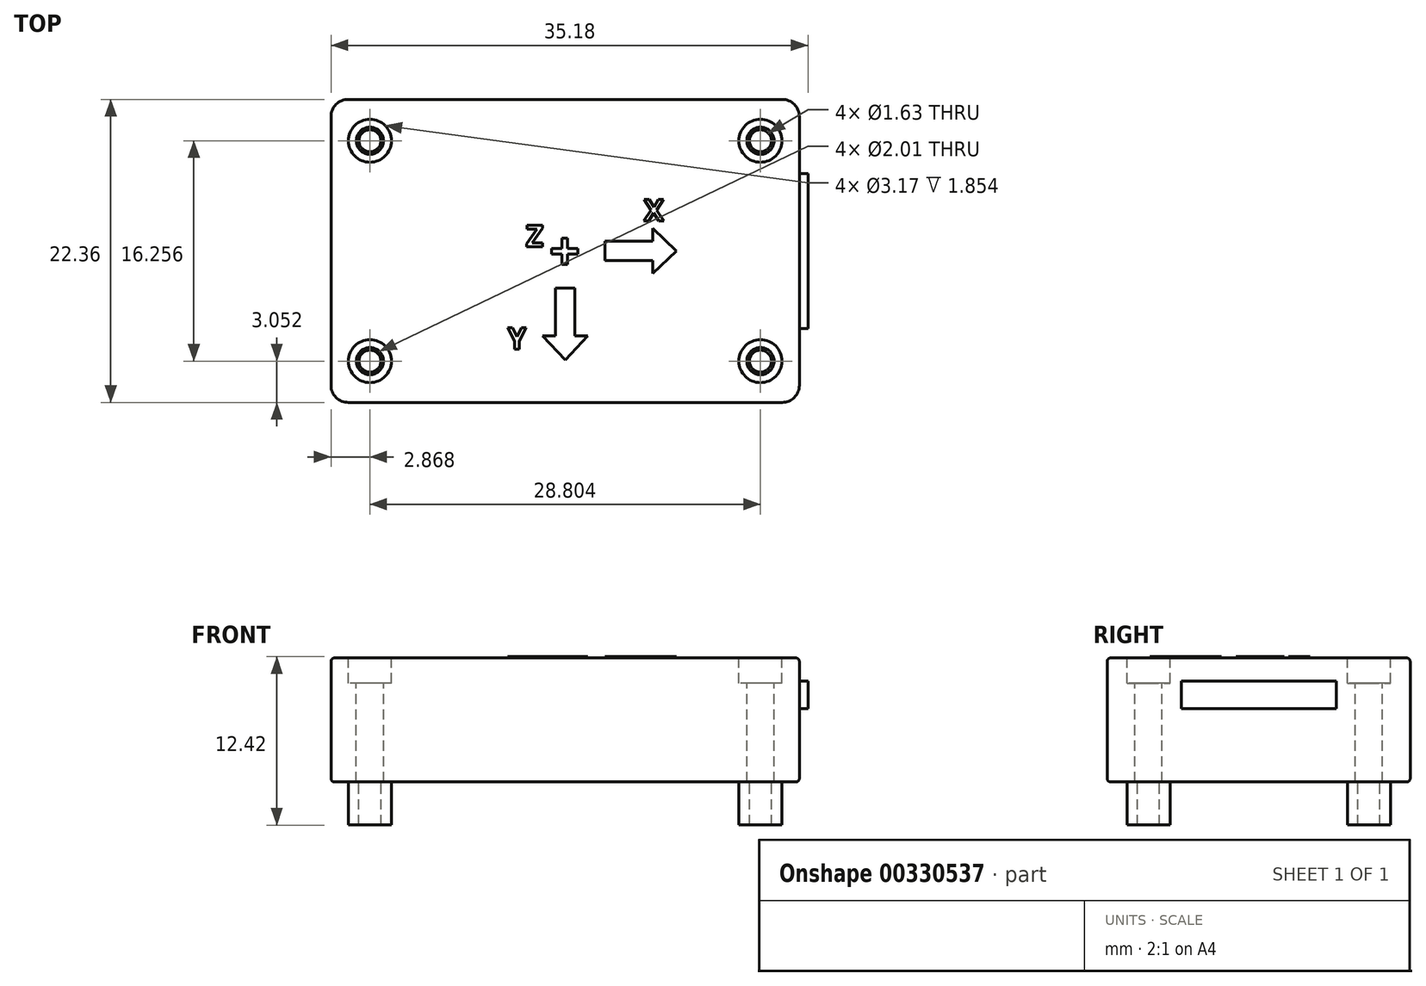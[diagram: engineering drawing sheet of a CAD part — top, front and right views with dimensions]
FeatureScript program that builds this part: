
annotation { "Feature Type Name" : "Feature", "Feature Type Description" : "" }
export const myFeature = defineFeature(function(context is Context, id is Id, definition is map)
    precondition{}
    {
        {
            var Q0;
            Q0=qCreatedBy(makeId("Top.planeOp"),FACE);
            var sketch = newSketch(context, id + "F0", { "sketchPlane" : qUnion([Q0])});
            skLineSegment(sketch, "E0.bottom", {"start": v(16, -11.18) * mm, "end": v(-16, -11.18) * mm});
            skLineSegment(sketch, "E0.top", {"start": v(16, 11.18) * mm, "end": v(-16, 11.18) * mm});
            skLineSegment(sketch, "E0.left", {"start": v(17.27, -9.9) * mm, "end": v(17.27, 9.9) * mm});
            skLineSegment(sketch, "E0.right", {"start": v(-17.27, -9.9) * mm, "end": v(-17.27, 9.9) * mm});
            skPoint(sketch, "E0.middle", {"position": v(0, 0) * mm});
            skPoint(sketch, "E1.visualSharp", {"position": v(-17.27, 11.18) * mm});
            skArc(sketch, "E1.filletArc", {"start": v(-16, 11.18) * mm, "mid": v(-16.9, 10.8) * mm, "end": v(-17.27, 9.9) * mm});
            skPoint(sketch, "E2.visualSharp", {"position": v(17.27, 11.18) * mm});
            skArc(sketch, "E2.filletArc", {"start": v(17.27, 9.9) * mm, "mid": v(16.9, 10.8) * mm, "end": v(16, 11.18) * mm});
            skPoint(sketch, "E3.visualSharp", {"position": v(17.27, -11.18) * mm});
            skArc(sketch, "E3.filletArc", {"start": v(16, -11.18) * mm, "mid": v(16.9, -10.8) * mm, "end": v(17.27, -9.9) * mm});
            skPoint(sketch, "E4.visualSharp", {"position": v(-17.27, -11.18) * mm});
            skArc(sketch, "E4.filletArc", {"start": v(-17.27, -9.9) * mm, "mid": v(-16.9, -10.8) * mm, "end": v(-16, -11.18) * mm});
            skSolve(sketch);
        }
        {
            var Q0;
            Q0 = qSketchRegion(id + "F0", true);
            extrude(context, id + "F1", {"entities" : qUnion([Q0]), "depth" : 9.14 * mm, "offsetDistance" : 25.4 * mm});
        }
        {
            var Q0;
            Q0=makeQuery(id+"F1.opExtrude","CAP_EDGE",EDGE,{"disambiguationData":[OSD([sQuery(id+"F0.wireOp",EDGE,"E0.bottom")])],"isStart":false});
            var Q1;
            Q1=makeQuery(id+"F1.opExtrude","CAP_FACE",FACE,{"disambiguationData":[OSD([sQuery(id+"F0.wireOp",EDGE,"E0.bottom"),sQuery(id+"F0.wireOp",EDGE,"E0.top"),sQuery(id+"F0.wireOp",EDGE,"E0.left"),sQuery(id+"F0.wireOp",EDGE,"E0.right"),sQuery(id+"F0.wireOp",EDGE,"E1.filletArc"),sQuery(id+"F0.wireOp",EDGE,"E2.filletArc"),sQuery(id+"F0.wireOp",EDGE,"E3.filletArc"),sQuery(id+"F0.wireOp",EDGE,"E4.filletArc")])],"isStart":true});
            fillet(context, id + "F2", {"entities" : qUnion([Q0, Q1]), "radius" : 0.25 * mm, "tangentPropagation" : true, "allowEdgeOverflow" : false});
        }
        {
            var Q0;
            Q0=makeQuery(id+"F1.opExtrude","CAP_FACE",FACE,{"disambiguationData":[OSD([sQuery(id+"F0.wireOp",EDGE,"E0.bottom"),sQuery(id+"F0.wireOp",EDGE,"E0.top"),sQuery(id+"F0.wireOp",EDGE,"E0.left"),sQuery(id+"F0.wireOp",EDGE,"E0.right"),sQuery(id+"F0.wireOp",EDGE,"E1.filletArc"),sQuery(id+"F0.wireOp",EDGE,"E2.filletArc"),sQuery(id+"F0.wireOp",EDGE,"E3.filletArc"),sQuery(id+"F0.wireOp",EDGE,"E4.filletArc")])],"isStart":false});
            var sketch = newSketch(context, id + "F3", { "sketchPlane" : qUnion([Q0])});
            skLineSegment(sketch, "E5", {"start": v(0, 10.92) * mm, "end": v(0, -10.92) * mm, "construction": true});
            skLineSegment(sketch, "E6", {"start": v(-17.02, 0) * mm, "end": v(17.52, 0) * mm, "construction": true});
            skPoint(sketch, "E6.endSnap0", {"position": v(17.02, 0) * mm});
            skCircle(sketch, "E7", {"center": v(-14.4, 8.13) * mm, "radius": 1 * mm});
            skCircle(sketch, "E8.MirrorC", {"center": v(14.4, 8.13) * mm, "radius": 1 * mm});
            skLineSegment(sketch, "E9.MirrorCS", {"start": v(17.02, 0) * mm, "end": v(-17.52, 0) * mm, "construction": true});
            skCircle(sketch, "E10.MirrorC", {"center": v(-14.4, -8.13) * mm, "radius": 1 * mm});
            skCircle(sketch, "E11.MirrorC", {"center": v(14.4, -8.13) * mm, "radius": 1 * mm});
            skSolve(sketch);
        }
        {
            var Q0;
            Q0 = qSketchRegion(id + "F3", true);
            extrude(context, id + "F4", {"entities" : qUnion([Q0]), "operationType" : NewBodyOperationType.REMOVE, "endBound" : BoundingType.THROUGH_ALL, "oppositeDirection" : true, "depth" : 25.4 * mm, "offsetDistance" : 25.4 * mm});
        }
        {
            var Q0;
            Q0=makeQuery(id+"F1.opExtrude","CAP_FACE",FACE,{"disambiguationData":[OSD([sQuery(id+"F0.wireOp",EDGE,"E0.bottom"),sQuery(id+"F0.wireOp",EDGE,"E0.top"),sQuery(id+"F0.wireOp",EDGE,"E0.left"),sQuery(id+"F0.wireOp",EDGE,"E0.right"),sQuery(id+"F0.wireOp",EDGE,"E1.filletArc"),sQuery(id+"F0.wireOp",EDGE,"E2.filletArc"),sQuery(id+"F0.wireOp",EDGE,"E3.filletArc"),sQuery(id+"F0.wireOp",EDGE,"E4.filletArc")])],"isStart":false});
            var sketch = newSketch(context, id + "F5", { "sketchPlane" : qUnion([Q0])});
            skCircle(sketch, "E12", {"center": v(-14.4, 8.13) * mm, "radius": 1.59 * mm});
            skCircle(sketch, "E13", {"center": v(14.4, 8.13) * mm, "radius": 1.59 * mm});
            skCircle(sketch, "E14", {"center": v(14.4, -8.13) * mm, "radius": 1.59 * mm});
            skCircle(sketch, "E15", {"center": v(-14.4, -8.13) * mm, "radius": 1.59 * mm});
            skSolve(sketch);
        }
        {
            var Q0;
            Q0 = qSketchRegion(id + "F5", true);
            extrude(context, id + "F6", {"entities" : qUnion([Q0]), "operationType" : NewBodyOperationType.REMOVE, "oppositeDirection" : true, "depth" : 1.85 * mm, "offsetDistance" : 25.4 * mm});
        }
        {
            var Q0;
            Q0=makeQuery(id+"F1.opExtrude","SWEPT_FACE",FACE,{"disambiguationData":[OSD([sQuery(id+"F0.wireOp",EDGE,"E0.left")])]});
            var sketch = newSketch(context, id + "F7", { "sketchPlane" : qUnion([Q0])});
            skLineSegment(sketch, "E16", {"start": v(0, 8.9) * mm, "end": v(0, 0) * mm, "construction": true});
            skLineSegment(sketch, "E17", {"start": v(-11.07, 4.57) * mm, "end": v(11.58, 4.57) * mm, "construction": true});
            skPoint(sketch, "E17.startSnap0", {"position": v(-9.9, 4.57) * mm});
            skLineSegment(sketch, "E18.bottom", {"start": v(5.71, 5.4) * mm, "end": v(-5.71, 5.4) * mm});
            skLineSegment(sketch, "E18.top", {"start": v(5.71, 7.43) * mm, "end": v(-5.71, 7.43) * mm});
            skLineSegment(sketch, "E18.left", {"start": v(5.71, 5.4) * mm, "end": v(5.71, 7.43) * mm});
            skLineSegment(sketch, "E18.right", {"start": v(-5.71, 5.4) * mm, "end": v(-5.71, 7.43) * mm});
            skPoint(sketch, "E18.middle", {"position": v(0, 6.42) * mm});
            skSolve(sketch);
        }
        {
            var Q0;
            Q0 = qSketchRegion(id + "F7", true);
            extrude(context, id + "F8", {"entities" : qUnion([Q0]), "depth" : 0.64 * mm, "offsetDistance" : 25.4 * mm});
        }
        {
            var Q0;
            Q0=makeQuery(id+"F1.opExtrude","CAP_FACE",FACE,{"disambiguationData":[OSD([sQuery(id+"F0.wireOp",EDGE,"E0.bottom"),sQuery(id+"F0.wireOp",EDGE,"E0.top"),sQuery(id+"F0.wireOp",EDGE,"E0.left"),sQuery(id+"F0.wireOp",EDGE,"E0.right"),sQuery(id+"F0.wireOp",EDGE,"E1.filletArc"),sQuery(id+"F0.wireOp",EDGE,"E2.filletArc"),sQuery(id+"F0.wireOp",EDGE,"E3.filletArc"),sQuery(id+"F0.wireOp",EDGE,"E4.filletArc")])],"isStart":false});
            var sketch = newSketch(context, id + "F9", { "sketchPlane" : qUnion([Q0])});
            skText(sketch, "E19", { "text": "X", "fontName": "OpenSans-Bold.ttf"});
            skLineSegment(sketch, "E20", {"start": v(0, 0) * mm, "end": v(5.39, 0) * mm, "construction": true});
            skLineSegment(sketch, "E21", {"start": v(0, 0) * mm, "end": v(0, -3.11) * mm, "construction": true});
            skLineSegment(sketch, "E22", {"start": v(2.92, 0) * mm, "end": v(2.92, 0.72) * mm});
            skLineSegment(sketch, "E23", {"start": v(2.92, 0.72) * mm, "end": v(6.45, 0.72) * mm});
            skLineSegment(sketch, "E24", {"start": v(6.45, 0.72) * mm, "end": v(6.45, 1.67) * mm});
            skLineSegment(sketch, "E25", {"start": v(6.45, 1.67) * mm, "end": v(8.21, 0) * mm});
            skLineSegment(sketch, "E26.MirrorCS", {"start": v(6.45, -1.66) * mm, "end": v(8.21, 0) * mm});
            skLineSegment(sketch, "E27.MirrorCS", {"start": v(6.45, -0.71) * mm, "end": v(6.45, -1.66) * mm});
            skLineSegment(sketch, "E28.MirrorCS", {"start": v(2.92, 0) * mm, "end": v(2.92, -0.71) * mm});
            skLineSegment(sketch, "E29.MirrorCS", {"start": v(2.92, -0.71) * mm, "end": v(6.45, -0.71) * mm});
            skLineSegment(sketch, "E30", {"start": v(0, -2.75) * mm, "end": v(0.72, -2.75) * mm});
            skLineSegment(sketch, "E31", {"start": v(0.72, -2.75) * mm, "end": v(0.72, -6.27) * mm});
            skLineSegment(sketch, "E32", {"start": v(0.72, -6.27) * mm, "end": v(1.67, -6.27) * mm});
            skLineSegment(sketch, "E33", {"start": v(1.67, -6.27) * mm, "end": v(0, -8.04) * mm});
            skLineSegment(sketch, "E34.MirrorCS", {"start": v(-1.66, -6.27) * mm, "end": v(0, -8.04) * mm});
            skLineSegment(sketch, "E35.MirrorCS", {"start": v(-0.71, -6.27) * mm, "end": v(-1.66, -6.27) * mm});
            skLineSegment(sketch, "E36.MirrorCS", {"start": v(0, -2.75) * mm, "end": v(-0.71, -2.75) * mm});
            skLineSegment(sketch, "E37.MirrorCS", {"start": v(-0.71, -2.75) * mm, "end": v(-0.71, -6.27) * mm});
            skText(sketch, "E38", { "text": "Y", "fontName": "OpenSans-Bold.ttf"});
            skText(sketch, "E39", { "text": "Z", "fontName": "OpenSans-Bold.ttf"});
            skText(sketch, "E40", { "text": "+", "fontName": "OpenSans-Bold.ttf"});
            const initialGuessF9  = {"E19": [0.0058, 0.0022, 1, 0, 0.0016], "E38": [-0.00425, -0.00725, 1, 0, 0.0016], "E39": [-0.00289, 0.0003, 1, 0, 0.0016], "E40": [-0.00116, -0.00142, 1, 0, 0.00286]};
            skSetInitialGuess(sketch, initialGuessF9);
            skSolve(sketch);
        }
        {
            var Q0;
            Q0 = qSketchRegion(id + "F9", true);
            extrude(context, id + "F10", {"entities" : qUnion([Q0]), "depth" : .1 * mm, "offsetDistance" : 25 * mm});
        }
        {
            var Q0;
            Q0=makeQuery(id+"F1.opExtrude","CAP_FACE",FACE,{"disambiguationData":[OSD([sQuery(id+"F0.wireOp",EDGE,"E0.bottom"),sQuery(id+"F0.wireOp",EDGE,"E0.top"),sQuery(id+"F0.wireOp",EDGE,"E0.left"),sQuery(id+"F0.wireOp",EDGE,"E0.right"),sQuery(id+"F0.wireOp",EDGE,"E1.filletArc"),sQuery(id+"F0.wireOp",EDGE,"E2.filletArc"),sQuery(id+"F0.wireOp",EDGE,"E3.filletArc"),sQuery(id+"F0.wireOp",EDGE,"E4.filletArc")])],"isStart":true});
            var sketch = newSketch(context, id + "F11", { "sketchPlane" : qUnion([Q0])});
            skCircle(sketch, "E41", {"center": v(-14.4, 8.13) * mm, "radius": 0.81 * mm});
            skCircle(sketch, "E42", {"center": v(-14.4, 8.13) * mm, "radius": 1.59 * mm});
            skLineSegment(sketch, "E43", {"start": v(0, 10.92) * mm, "end": v(0, -10.92) * mm, "construction": true});
            skLineSegment(sketch, "E44", {"start": v(-17.02, 0) * mm, "end": v(17.02, 0) * mm, "construction": true});
            skCircle(sketch, "E45.MirrorC", {"center": v(14.4, 8.13) * mm, "radius": 1.59 * mm});
            skCircle(sketch, "E46.MirrorC", {"center": v(14.4, 8.13) * mm, "radius": 0.81 * mm});
            skLineSegment(sketch, "E47.MirrorCS", {"start": v(17.02, 0) * mm, "end": v(-17.02, 0) * mm, "construction": true});
            skCircle(sketch, "E48.MirrorC", {"center": v(-14.4, -8.13) * mm, "radius": 1.59 * mm});
            skCircle(sketch, "E49.MirrorC", {"center": v(-14.4, -8.13) * mm, "radius": 0.81 * mm});
            skCircle(sketch, "E50.MirrorC", {"center": v(14.4, -8.13) * mm, "radius": 0.81 * mm});
            skCircle(sketch, "E51.MirrorC", {"center": v(14.4, -8.13) * mm, "radius": 1.59 * mm});
            skSolve(sketch);
        }
        {
            var Q0;
            Q0 = qSketchRegion(id + "F11", true);
            extrude(context, id + "F12", {"entities" : qUnion([Q0]), "depth" : 3.17 * mm, "offsetDistance" : 25 * mm});
        }
    });
